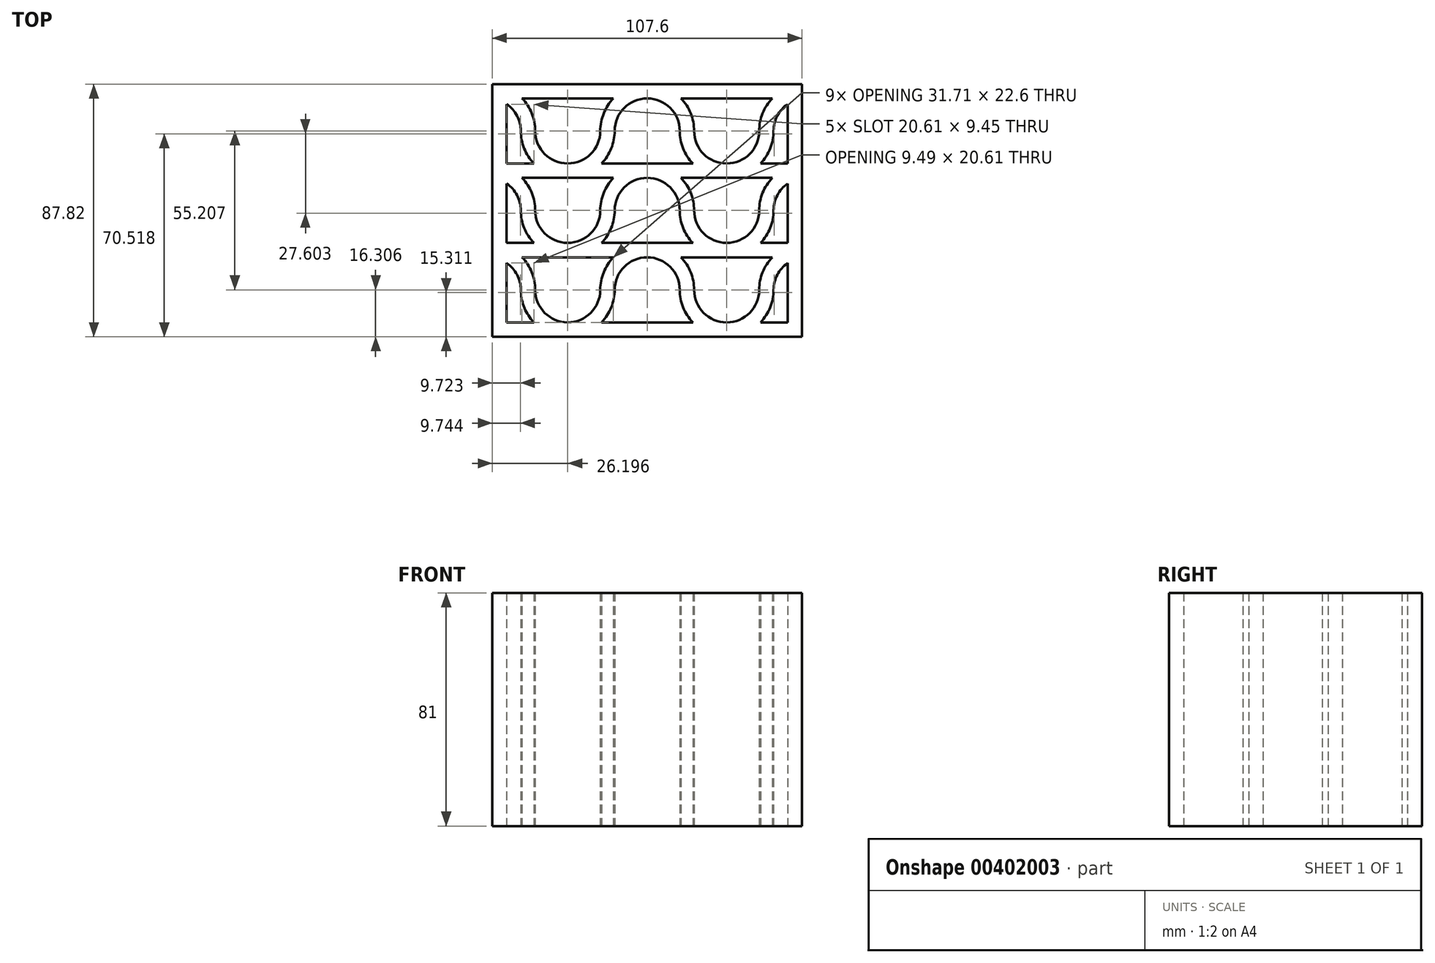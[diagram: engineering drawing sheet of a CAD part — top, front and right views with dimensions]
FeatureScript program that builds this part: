
annotation { "Feature Type Name" : "Feature", "Feature Type Description" : "" }
export const myFeature = defineFeature(function(context is Context, id is Id, definition is map)
    precondition{}
    {
        {
            var Q0;
            Q0=qCreatedBy(makeId("Top.planeOp"),FACE);
            var sketch = newSketch(context, id + "F0", { "sketchPlane" : qUnion([Q0])});
            skLineSegment(sketch, "E0.bottom", {"start": v(53.8, 43.9) * mm, "end": v(-53.8, 43.9) * mm});
            skLineSegment(sketch, "E0.top", {"start": v(53.8, -43.9) * mm, "end": v(-53.8, -43.9) * mm});
            skLineSegment(sketch, "E0.left", {"start": v(53.8, 43.9) * mm, "end": v(53.8, -43.9) * mm});
            skLineSegment(sketch, "E0.right", {"start": v(-53.8, 43.9) * mm, "end": v(-53.8, -43.9) * mm});
            skPoint(sketch, "E0.middle", {"position": v(0, 0) * mm});
            skLineSegment(sketch, "E1.top", {"start": v(-48.8, -38.9) * mm, "end": v(-39.31, -38.9) * mm});
            skLineSegment(sketch, "E1.left", {"start": v(-48.8, 36.91) * mm, "end": v(-48.8, 16.3) * mm});
            skLineSegment(sketch, "E1.right", {"start": v(48.8, 36.91) * mm, "end": v(48.8, 27.6) * mm});
            skLineSegment(sketch, "E2", {"start": v(0, 107) * mm, "end": v(0, -111.2) * mm, "construction": true});
            skPoint(sketch, "E2.startSnap0", {"position": v(0, 43.9) * mm});
            skLineSegment(sketch, "E3", {"start": v(-121.2, 0) * mm, "end": v(167.99, 0) * mm, "construction": true});
            skLineSegment(sketch, "E4", {"start": v(0, 43.9) * mm, "end": v(0, 38.9) * mm, "construction": true});
            skLineSegment(sketch, "E5", {"start": v(0, 41.4) * mm, "end": v(-82.57, 41.4) * mm, "construction": true});
            skLineSegment(sketch, "E6", {"start": v(0, 41.4) * mm, "end": v(79.47, 41.4) * mm, "construction": true});
            skLineSegment(sketch, "E7", {"start": v(0, -38.9) * mm, "end": v(0, -43.9) * mm, "construction": true});
            skLineSegment(sketch, "E8", {"start": v(0, -41.4) * mm, "end": v(-71.82, -41.4) * mm, "construction": true});
            skLineSegment(sketch, "E9", {"start": v(0, -41.4) * mm, "end": v(82.38, -41.4) * mm, "construction": true});
            skLineSegment(sketch, "E10.top", {"start": v(43.46, 11.3) * mm, "end": v(11.75, 11.3) * mm});
            skPoint(sketch, "E10.middle", {"position": v(0, 13.8) * mm});
            skLineSegment(sketch, "E11.bottom", {"start": v(-48.8, -11.3) * mm, "end": v(-39.35, -11.3) * mm});
            skLineSegment(sketch, "E11.top", {"start": v(-43.46, -16.3) * mm, "end": v(-11.75, -16.3) * mm});
            skPoint(sketch, "E11.middle", {"position": v(0, -13.8) * mm});
            skLineSegment(sketch, "E12", {"start": v(0, 16.3) * mm, "end": v(0, 11.3) * mm, "construction": true});
            skLineSegment(sketch, "E13", {"start": v(0, 13.8) * mm, "end": v(-70.02, 13.8) * mm, "construction": true});
            skLineSegment(sketch, "E14", {"start": v(0, 13.8) * mm, "end": v(116.67, 13.8) * mm, "construction": true});
            skLineSegment(sketch, "E15", {"start": v(0, -11.3) * mm, "end": v(0, -16.3) * mm, "construction": true});
            skLineSegment(sketch, "E16", {"start": v(0, -13.8) * mm, "end": v(-72.75, -13.8) * mm, "construction": true});
            skLineSegment(sketch, "E17", {"start": v(0, -13.8) * mm, "end": v(120.57, -13.8) * mm, "construction": true});
            skLineSegment(sketch, "E18", {"start": v(-53.8, 27.6) * mm, "end": v(-48.8, 27.6) * mm, "construction": true});
            skLineSegment(sketch, "E19", {"start": v(-48.8, 16.3) * mm, "end": v(-39.35, 16.3) * mm});
            skLineSegment(sketch, "E20", {"start": v(-43.46, 38.9) * mm, "end": v(-11.75, 38.9) * mm});
            skLineSegment(sketch, "E21", {"start": v(0, 38.9) * mm, "end": v(0, 16.3) * mm, "construction": true});
            skArc(sketch, "E22", {"start": v(11.3, 27.6) * mm, "mid": v(0, 38.9) * mm, "end": v(-11.3, 27.6) * mm});
            skLineSegment(sketch, "E23", {"start": v(-65.91, 27.6) * mm, "end": v(64.87, 27.6) * mm, "construction": true});
            skArc(sketch, "E24", {"start": v(11.3, 27.6) * mm, "mid": v(12.48, 21.52) * mm, "end": v(15.85, 16.31) * mm});
            skArc(sketch, "E25", {"start": v(16.3, 27.6) * mm, "mid": v(27.6, 16.3) * mm, "end": v(38.9, 27.6) * mm});
            skArc(sketch, "E26", {"start": v(43.45, 16.31) * mm, "mid": v(43.45, 16.3) * mm, "end": v(43.46, 16.3) * mm});
            skArc(sketch, "E27", {"start": v(48.8, 36.91) * mm, "mid": v(45.2, 32.86) * mm, "end": v(43.9, 27.6) * mm});
            skArc(sketch, "E28", {"start": v(-43.9, 27.6) * mm, "mid": v(-42.72, 21.51) * mm, "end": v(-39.35, 16.3) * mm});
            skArc(sketch, "E29", {"start": v(-38.9, 27.6) * mm, "mid": v(-27.6, 16.3) * mm, "end": v(-16.3, 27.6) * mm});
            skArc(sketch, "E30", {"start": v(-43.46, 16.3) * mm, "mid": v(-43.45, 16.3) * mm, "end": v(-43.45, 16.31) * mm});
            skArc(sketch, "E31", {"start": v(-43.9, 27.6) * mm, "mid": v(-45.2, 32.86) * mm, "end": v(-48.8, 36.91) * mm});
            skArc(sketch, "E32.trimOffspring", {"start": v(-38.9, 27.6) * mm, "mid": v(-40.09, 33.7) * mm, "end": v(-43.46, 38.9) * mm});
            skArc(sketch, "E33.trimOffspring", {"start": v(-15.86, 16.3) * mm, "mid": v(-12.48, 21.51) * mm, "end": v(-11.3, 27.6) * mm});
            skArc(sketch, "E34.trimOffspring", {"start": v(-15.85, 38.9) * mm, "mid": v(-15.85, 38.9) * mm, "end": v(-15.86, 38.9) * mm});
            skArc(sketch, "E35.trimOffspring", {"start": v(-11.75, 38.9) * mm, "mid": v(-15.12, 33.7) * mm, "end": v(-16.3, 27.6) * mm});
            skArc(sketch, "E36.trimOffspring", {"start": v(16.3, 27.6) * mm, "mid": v(15.12, 33.7) * mm, "end": v(11.75, 38.9) * mm});
            skArc(sketch, "E37.trimOffspring", {"start": v(15.86, 38.9) * mm, "mid": v(15.85, 38.9) * mm, "end": v(15.85, 38.9) * mm});
            skArc(sketch, "E38.trimOffspring", {"start": v(39.35, 16.3) * mm, "mid": v(42.72, 21.51) * mm, "end": v(43.9, 27.6) * mm});
            skArc(sketch, "E39.trimOffspring", {"start": v(43.46, 38.9) * mm, "mid": v(40.09, 33.7) * mm, "end": v(38.9, 27.6) * mm});
            skPoint(sketch, "E40.orphan", {"position": v(-48.8, 38.9) * mm});
            skLineSegment(sketch, "E41.trimOffspring", {"start": v(-15.86, 16.3) * mm, "end": v(15.86, 16.3) * mm});
            skLineSegment(sketch, "E42.trimOffspring", {"start": v(11.75, 38.9) * mm, "end": v(43.46, 38.9) * mm});
            skArc(sketch, "E43", {"start": v(15.85, 16.31) * mm, "mid": v(15.85, 16.3) * mm, "end": v(15.86, 16.3) * mm});
            skLineSegment(sketch, "E44.trimOffspring", {"start": v(39.35, 16.3) * mm, "end": v(48.8, 16.3) * mm});
            skPoint(sketch, "E45.orphan", {"position": v(48.8, 38.9) * mm});
            skLineSegment(sketch, "E46", {"start": v(0, 11.3) * mm, "end": v(0, -11.3) * mm, "construction": true});
            skArc(sketch, "E47", {"start": v(11.3, 0) * mm, "mid": v(0, 11.3) * mm, "end": v(-11.3, 0) * mm});
            skArc(sketch, "E48", {"start": v(11.3, 0) * mm, "mid": v(12.48, -6.09) * mm, "end": v(15.85, -11.3) * mm});
            skArc(sketch, "E49", {"start": v(16.3, 0) * mm, "mid": v(27.6, -11.3) * mm, "end": v(38.9, 0) * mm});
            skArc(sketch, "E50", {"start": v(43.45, -11.3) * mm, "mid": v(43.45, -11.3) * mm, "end": v(43.46, -11.3) * mm});
            skArc(sketch, "E51", {"start": v(48.8, 9.31) * mm, "mid": v(45.2, 5.26) * mm, "end": v(43.9, 0) * mm});
            skArc(sketch, "E52", {"start": v(-43.9, 0) * mm, "mid": v(-42.72, -6.1) * mm, "end": v(-39.35, -11.3) * mm});
            skArc(sketch, "E53", {"start": v(-38.9, 0) * mm, "mid": v(-27.6, -11.3) * mm, "end": v(-16.3, 0) * mm});
            skArc(sketch, "E54", {"start": v(-43.46, -11.3) * mm, "mid": v(-43.45, -11.3) * mm, "end": v(-43.45, -11.3) * mm});
            skArc(sketch, "E55.trimOffspring", {"start": v(-43.9, 0) * mm, "mid": v(-45.2, 5.26) * mm, "end": v(-48.8, 9.31) * mm});
            skArc(sketch, "E56.trimOffspring", {"start": v(-38.9, 0) * mm, "mid": v(-40.09, 6.1) * mm, "end": v(-43.46, 11.3) * mm});
            skArc(sketch, "E57.trimOffspring", {"start": v(-15.86, -11.3) * mm, "mid": v(-12.48, -6.1) * mm, "end": v(-11.3, 0) * mm});
            skArc(sketch, "E58.trimOffspring", {"start": v(-15.85, 11.3) * mm, "mid": v(-15.85, 11.3) * mm, "end": v(-15.86, 11.3) * mm});
            skArc(sketch, "E59.trimOffspring", {"start": v(-11.75, 11.3) * mm, "mid": v(-15.12, 6.1) * mm, "end": v(-16.3, 0) * mm});
            skArc(sketch, "E60.trimOffspring", {"start": v(16.3, 0) * mm, "mid": v(15.12, 6.1) * mm, "end": v(11.75, 11.3) * mm});
            skArc(sketch, "E61.trimOffspring", {"start": v(39.35, -11.3) * mm, "mid": v(42.72, -6.1) * mm, "end": v(43.9, 0) * mm});
            skArc(sketch, "E62.trimOffspring", {"start": v(15.86, 11.3) * mm, "mid": v(15.85, 11.3) * mm, "end": v(15.85, 11.3) * mm});
            skArc(sketch, "E63.trimOffspring", {"start": v(43.46, 11.3) * mm, "mid": v(40.09, 6.1) * mm, "end": v(38.9, 0) * mm});
            skLineSegment(sketch, "E64.trimOffspring", {"start": v(-48.8, 9.31) * mm, "end": v(-48.8, -11.3) * mm});
            skPoint(sketch, "E65.trimOffspring.end.orphan", {"position": v(-48.8, 11.3) * mm});
            skLineSegment(sketch, "E66.trimOffspring", {"start": v(-11.75, 11.3) * mm, "end": v(-43.46, 11.3) * mm});
            skLineSegment(sketch, "E67.trimOffspring", {"start": v(-15.86, -11.3) * mm, "end": v(15.86, -11.3) * mm});
            skArc(sketch, "E68", {"start": v(15.85, -11.3) * mm, "mid": v(15.85, -11.3) * mm, "end": v(15.86, -11.3) * mm});
            skLineSegment(sketch, "E69.trimOffspring", {"start": v(39.35, -11.3) * mm, "end": v(48.8, -11.3) * mm});
            skLineSegment(sketch, "E70.trimOffspring", {"start": v(48.8, 9.31) * mm, "end": v(48.8, -11.3) * mm});
            skPoint(sketch, "E71.trimOffspring.end.orphan", {"position": v(48.8, 11.3) * mm});
            skLineSegment(sketch, "E72", {"start": v(0, -16.3) * mm, "end": v(0, -38.9) * mm, "construction": true});
            skArc(sketch, "E73", {"start": v(11.3, -27.6) * mm, "mid": v(0, -16.3) * mm, "end": v(-11.3, -27.6) * mm});
            skArc(sketch, "E74", {"start": v(16.3, -27.6) * mm, "mid": v(15.12, -21.51) * mm, "end": v(11.75, -16.3) * mm});
            skArc(sketch, "E75", {"start": v(11.3, -27.6) * mm, "mid": v(12.48, -33.7) * mm, "end": v(15.86, -38.9) * mm});
            skArc(sketch, "E76", {"start": v(16.3, -27.6) * mm, "mid": v(27.6, -38.9) * mm, "end": v(38.9, -27.6) * mm});
            skArc(sketch, "E77", {"start": v(43.45, -38.9) * mm, "mid": v(43.45, -38.9) * mm, "end": v(43.46, -38.9) * mm});
            skArc(sketch, "E78", {"start": v(48.8, -18.3) * mm, "mid": v(45.2, -22.34) * mm, "end": v(43.9, -27.6) * mm});
            skArc(sketch, "E79", {"start": v(-43.9, -27.6) * mm, "mid": v(-42.9, -33.25) * mm, "end": v(-39.99, -38.2) * mm});
            skArc(sketch, "E80", {"start": v(-38.9, -27.6) * mm, "mid": v(-27.6, -38.9) * mm, "end": v(-16.3, -27.6) * mm});
            skArc(sketch, "E81", {"start": v(-43.46, -38.9) * mm, "mid": v(-43.45, -38.9) * mm, "end": v(-43.45, -38.9) * mm});
            skArc(sketch, "E82", {"start": v(-43.9, -27.6) * mm, "mid": v(-45.2, -22.34) * mm, "end": v(-48.8, -18.3) * mm});
            skArc(sketch, "E83.trimOffspring", {"start": v(-38.9, -27.6) * mm, "mid": v(-40.09, -21.51) * mm, "end": v(-43.46, -16.3) * mm});
            skArc(sketch, "E84.trimOffspring", {"start": v(-15.86, -38.9) * mm, "mid": v(-12.48, -33.7) * mm, "end": v(-11.3, -27.6) * mm});
            skArc(sketch, "E85.trimOffspring", {"start": v(-11.75, -16.3) * mm, "mid": v(-15.12, -21.51) * mm, "end": v(-16.3, -27.6) * mm});
            skArc(sketch, "E86.trimOffspring", {"start": v(39.35, -38.9) * mm, "mid": v(42.72, -33.7) * mm, "end": v(43.9, -27.6) * mm});
            skLineSegment(sketch, "E87.trimOffspring", {"start": v(39.35, -38.9) * mm, "end": v(48.8, -38.9) * mm});
            skArc(sketch, "E88.trimOffspring", {"start": v(43.46, -16.3) * mm, "mid": v(40.09, -21.51) * mm, "end": v(38.9, -27.6) * mm});
            skLineSegment(sketch, "E89.trimOffspring", {"start": v(-48.8, -18.3) * mm, "end": v(-48.8, -38.9) * mm});
            skPoint(sketch, "E90.trimOffspring.end.orphan", {"position": v(-48.8, -16.3) * mm});
            skArc(sketch, "E91", {"start": v(-39.99, -38.2) * mm, "mid": v(-39.66, -38.57) * mm, "end": v(-39.31, -38.9) * mm});
            skLineSegment(sketch, "E92.trimOffspring", {"start": v(-15.86, -38.9) * mm, "end": v(15.86, -38.9) * mm});
            skLineSegment(sketch, "E93.trimOffspring", {"start": v(11.75, -16.3) * mm, "end": v(43.46, -16.3) * mm});
            skLineSegment(sketch, "E94.trimOffspring", {"start": v(48.8, -18.3) * mm, "end": v(48.8, -38.9) * mm});
            skPoint(sketch, "E95.trimOffspring.end.orphan", {"position": v(48.8, -16.3) * mm});
            skLineSegment(sketch, "E96", {"start": v(48.8, 27.6) * mm, "end": v(48.8, 16.3) * mm});
            skSolve(sketch);
        }
        {
            var Q0;
            Q0 = qSketchRegion(id + "F0", true);
            extrude(context, id + "F1", {"entities" : qUnion([Q0]), "depth" : 81 * mm});
        }
    });
